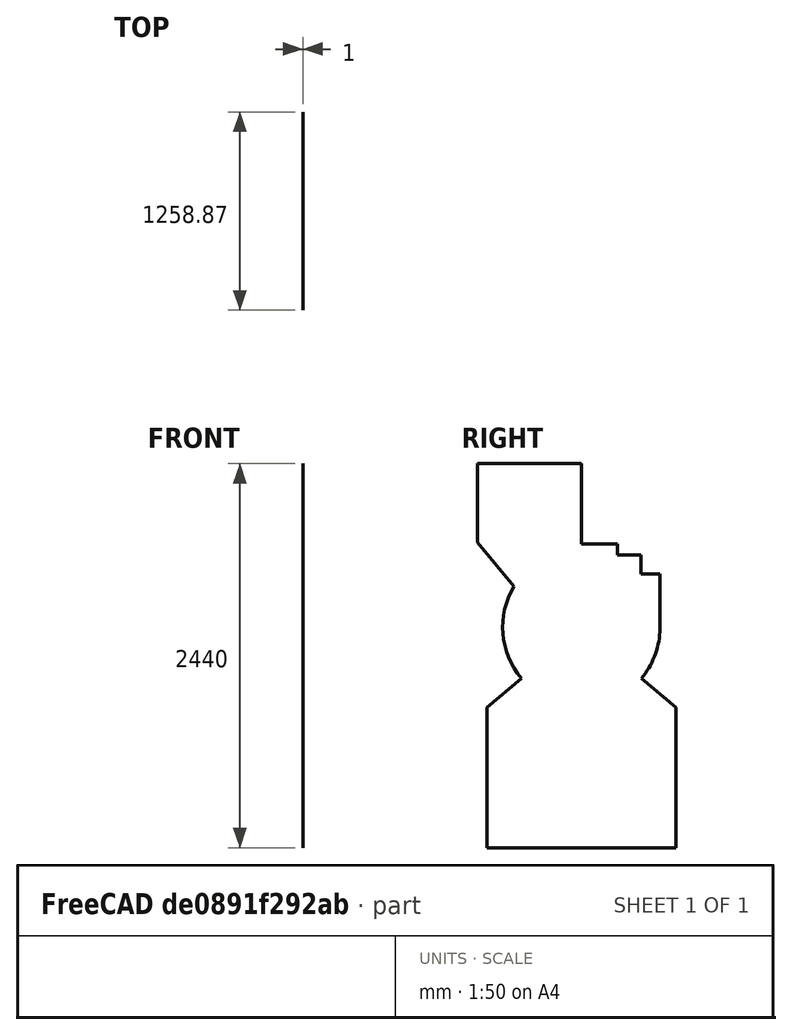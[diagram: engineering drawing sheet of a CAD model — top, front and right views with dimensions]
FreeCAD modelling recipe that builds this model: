
FCSTD DOCUMENT
Label: Shell_front
objects: Sketcher::SketchObject×1, PartDesign::Pad×1
note: 3 computed .brp shape members not serialized (recipe doc carries the construction recipe); baked Part::Feature solids carry a one-line shape summary decoded from their .brp

FEATURE [Sketcher::SketchObject] Sketch  label="Shell_front"
  Placement = pos=(500,0,0) rot=(0.57735,0.57735,0.57735;2.0944rad)
  sketch-geometry (17):
    g0: ArcOfCircle CenterX=0 CenterY=0 CenterZ=0 NormalX=0 NormalY=0 NormalZ=1 Radius=500 StartAngle=2.59474 EndAngle=3.84621
    g1: LineSegment StartX=-427.083 StartY=260 StartZ=0 EndX=-658.874 EndY=540 EndZ=0
    g2: LineSegment StartX=0 StartY=530 StartZ=0 EndX=230 EndY=530 EndZ=0
    g3: LineSegment StartX=230 StartY=530 StartZ=0 EndX=230 EndY=460 EndZ=0
    g4: LineSegment StartX=230 StartY=460 StartZ=0 EndX=380 EndY=460 EndZ=0
    g5: LineSegment StartX=380 StartY=460 StartZ=0 EndX=380 EndY=340 EndZ=0
    g6: LineSegment StartX=380 StartY=340 StartZ=0 EndX=499.099 EndY=340 EndZ=0
    g7: LineSegment StartX=499.099 StartY=340 StartZ=0 EndX=499.099 EndY=-30 EndZ=0
    g8: LineSegment StartX=-658.874 StartY=1040 StartZ=0 EndX=-658.874 EndY=540 EndZ=0
    g9: LineSegment StartX=-380.931 StartY=-323.87 StartZ=0 EndX=-600 EndY=-507.691 EndZ=0
    g10: LineSegment StartX=-600 StartY=-507.691 StartZ=0 EndX=-600 EndY=-1400 EndZ=0
    g11: LineSegment StartX=-600 StartY=-1400 StartZ=0 EndX=600 EndY=-1400 EndZ=0
    g12: LineSegment StartX=600 StartY=-1400 StartZ=0 EndX=600 EndY=-507.691 EndZ=0
    g13: LineSegment StartX=600 StartY=-507.691 StartZ=0 EndX=380.931 EndY=-323.87 EndZ=0
    g14: ArcOfCircle CenterX=0 CenterY=0 CenterZ=0 NormalX=0 NormalY=0 NormalZ=1 Radius=500 StartAngle=5.57857 EndAngle=6.22315
    g15: LineSegment StartX=-658.874 StartY=1040 StartZ=0 EndX=0 EndY=1040 EndZ=0
    g16: LineSegment StartX=0 StartY=1040 StartZ=0 EndX=0 EndY=530 EndZ=0
  constraints (52):
    c: Radius(g0) = 500
    c: DistanceX(g0) = 0
    c: DistanceY(g0) = 0
    c: Horizontal(g2)
    c: Vertical(g3)
    c: Coincident(g4,g3)
    c: Horizontal(g4)
    c: Vertical(g5)
    c: Coincident(g6,g5)
    c: Horizontal(g6)
    c: DistanceY(g1) = 540
    c: Coincident(g2,g3)
    c: Coincident(g4,g5)
    c: Coincident(g7,g14)
    c: Vertical(g7)
    c: Distance(g7) = 370
    c: Coincident(g1,g0)
    c: Coincident(g8,g1)
    c: Vertical(g8)
    c: Distance(g1) = 363.493
    c: Distance(g8) = 500
    c: Coincident(g10,g9)
    c: Vertical(g10)
    c: Horizontal(g11)
    c: Coincident(g12,g11)
    c: Vertical(g12)
    c: Coincident(g13,g12)
    c: Coincident(g11,g10)
    c: Equal(g12,g10)
    c: DistanceX(g11) = 600
    c: DistanceY(g11) = -1400
    c: Angle(g10,g9) = 2.26893
    c: Angle(g13,g12) = 2.26893
    c: Distance(g10) = 892.309
    c: Distance(g11) = 1200
    c: Coincident(g0,g14)
    c: Coincident(g15,g8)
    c: Horizontal(g15)
    c: Coincident(g16,g15)
    c: Vertical(g16)
    c: Coincident(g6,g7)
    c: Coincident(g16,g2)
    c: DistanceX(g5) = 380
    c: DistanceY(g5) = 340
    c: DistanceX(g3) = 230
    c: DistanceY(g3) = 460
    c: DistanceX(g2) = 0
    c: DistanceY(g2) = 530
    c: DistanceY(g0) = 260
    c: Coincident(g9,g0)
    c: Radius(g14) = 500
    c: Coincident(g14,g13)
FEATURE [PartDesign::Pad] Pad  label="Shell_front_"
  Length = 1
  MirroredExtent = false
  Sketch = -> Sketch
